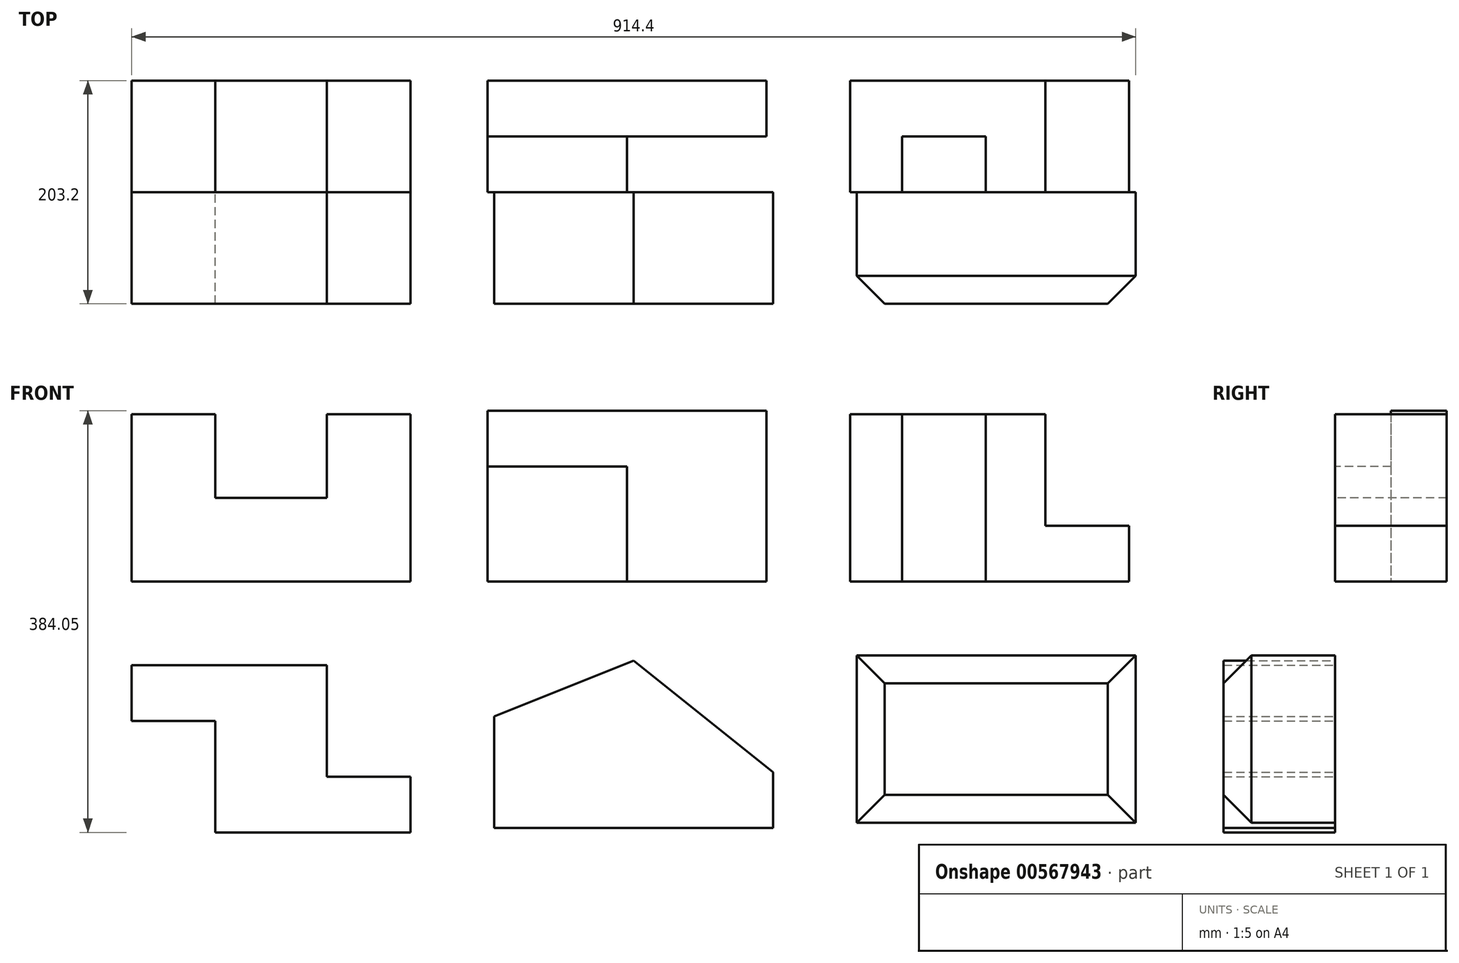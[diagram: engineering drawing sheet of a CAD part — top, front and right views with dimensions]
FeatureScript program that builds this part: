
annotation { "Feature Type Name" : "Feature", "Feature Type Description" : "" }
export const myFeature = defineFeature(function(context is Context, id is Id, definition is map)
    precondition{}
    {
        {
            var Q0;
            Q0=qCreatedBy(makeId("Front.planeOp"),FACE);
            var sketch = newSketch(context, id + "F0", { "sketchPlane" : qUnion([Q0])});
            skLineSegment(sketch, "E0", {"start": v(0, 0) * mm, "end": v(254, 0) * mm});
            skLineSegment(sketch, "E1", {"start": v(254, 0) * mm, "end": v(254, 152.4) * mm});
            skLineSegment(sketch, "E2", {"start": v(254, 152.4) * mm, "end": v(177.8, 152.4) * mm});
            skLineSegment(sketch, "E3", {"start": v(177.8, 152.4) * mm, "end": v(177.8, 76.2) * mm});
            skLineSegment(sketch, "E4", {"start": v(177.8, 76.2) * mm, "end": v(76.2, 76.2) * mm});
            skLineSegment(sketch, "E5", {"start": v(76.2, 76.2) * mm, "end": v(76.2, 152.4) * mm});
            skLineSegment(sketch, "E6", {"start": v(76.2, 152.4) * mm, "end": v(0, 152.4) * mm});
            skLineSegment(sketch, "E7", {"start": v(0, 152.4) * mm, "end": v(0, 0) * mm});
            skSolve(sketch);
        }
        {
            var Q0;
            Q0 = qSketchRegion(id + "F0", true);
            extrude(context, id + "F1", {"entities" : qUnion([Q0]), "oppositeDirection" : true, "depth" : 101.6 * mm, "offsetDistance" : 25.4 * mm});
        }
        {
            var Q0;
            Q0=qCreatedBy(makeId("Top.planeOp"),FACE);
            var sketch = newSketch(context, id + "F2", { "sketchPlane" : qUnion([Q0])});
            skLineSegment(sketch, "E8", {"start": v(323.96, 0) * mm, "end": v(323.96, 101.6) * mm});
            skLineSegment(sketch, "E9", {"start": v(323.96, 101.6) * mm, "end": v(577.96, 101.6) * mm});
            skLineSegment(sketch, "E10", {"start": v(577.96, 101.6) * mm, "end": v(577.96, 50.8) * mm});
            skLineSegment(sketch, "E11", {"start": v(577.96, 50.8) * mm, "end": v(450.96, 50.8) * mm});
            skLineSegment(sketch, "E12", {"start": v(450.96, 50.8) * mm, "end": v(450.96, 0) * mm});
            skLineSegment(sketch, "E13", {"start": v(450.96, 0) * mm, "end": v(323.96, 0) * mm});
            skSolve(sketch);
        }
        {
            var Q0;
            Q0=makeQuery(id+"F2.imprint","IMPRINT",FACE,{"disambiguationData":[TD([[makeQuery(id+"F2.imprint","IMPRINT",EDGE,{"derivedFrom":sQuery(id+"F2.wireOp",EDGE,"E8")}),-1.0]])]});
            extrude(context, id + "F3", {"entities" : qUnion([Q0]), "depth" : 155.45 * mm, "offsetDistance" : 25.4 * mm});
        }
        {
            var Q0;
            Q0=makeQuery(id+"F3.opExtrude","SWEPT_FACE",FACE,{"disambiguationData":[OSD([sQuery(id+"F2.wireOp",EDGE,"E13")])]});
            var sketch = newSketch(context, id + "F4", { "sketchPlane" : qUnion([Q0])});
            skLineSegment(sketch, "E14.bottom", {"start": v(323.96, 155.45) * mm, "end": v(450.96, 155.45) * mm});
            skLineSegment(sketch, "E14.top", {"start": v(323.96, 119.83) * mm, "end": v(450.96, 119.83) * mm});
            skLineSegment(sketch, "E14.left", {"start": v(323.96, 155.45) * mm, "end": v(323.96, 119.83) * mm});
            skLineSegment(sketch, "E14.right", {"start": v(450.96, 155.45) * mm, "end": v(450.96, 119.83) * mm});
            skSolve(sketch);
        }
        {
            var Q0;
            Q0 = qSketchRegion(id + "F4", true);
            extrude(context, id + "F5", {"entities" : qUnion([Q0]), "operationType" : NewBodyOperationType.ADD, "oppositeDirection" : true, "depth" : 50.8 * mm, "offsetDistance" : 25.4 * mm});
        }
        {
            var Q0;
            Q0=makeQuery(id+"F3.opExtrude","SWEPT_FACE",FACE,{"disambiguationData":[OSD([sQuery(id+"F2.wireOp",EDGE,"E13")])]});
            var sketch = newSketch(context, id + "F6", { "sketchPlane" : qUnion([Q0])});
            skLineSegment(sketch, "E15.bottom", {"start": v(323.96, 155.45) * mm, "end": v(450.96, 155.45) * mm});
            skLineSegment(sketch, "E15.top", {"start": v(323.96, 104.65) * mm, "end": v(450.96, 104.65) * mm});
            skLineSegment(sketch, "E15.left", {"start": v(323.96, 155.45) * mm, "end": v(323.96, 104.65) * mm});
            skLineSegment(sketch, "E15.right", {"start": v(450.96, 155.45) * mm, "end": v(450.96, 104.65) * mm});
            skSolve(sketch);
        }
        {
            var Q0;
            Q0=makeQuery(id+"F6.imprint","IMPRINT",FACE,{"disambiguationData":[TD([[makeQuery(id+"F6.imprint","IMPRINT",EDGE,{"derivedFrom":sQuery(id+"F6.wireOp",EDGE,"E15.bottom")}),1.0]])]});
            extrude(context, id + "F7", {"entities" : qUnion([Q0]), "operationType" : NewBodyOperationType.REMOVE, "oppositeDirection" : true, "depth" : 50.8 * mm, "offsetDistance" : 25.4 * mm});
        }
        {
            var Q0;
            Q0=qCreatedBy(makeId("Front.planeOp"),FACE);
            var sketch = newSketch(context, id + "F8", { "sketchPlane" : qUnion([Q0])});
            skLineSegment(sketch, "E16", {"start": v(654.16, 0) * mm, "end": v(654.16, 152.4) * mm});
            skLineSegment(sketch, "E17", {"start": v(654.16, 0) * mm, "end": v(908.16, 0) * mm});
            skLineSegment(sketch, "E18", {"start": v(908.16, 0) * mm, "end": v(908.16, 50.8) * mm});
            skLineSegment(sketch, "E19", {"start": v(908.16, 50.8) * mm, "end": v(831.96, 50.8) * mm});
            skLineSegment(sketch, "E20", {"start": v(831.96, 50.8) * mm, "end": v(831.96, 152.4) * mm});
            skLineSegment(sketch, "E21", {"start": v(831.96, 152.4) * mm, "end": v(654.16, 152.4) * mm});
            skSolve(sketch);
        }
        {
            var Q0;
            Q0=makeQuery(id+"F8.imprint","IMPRINT",FACE,{"disambiguationData":[TD([[makeQuery(id+"F8.imprint","IMPRINT",EDGE,{"derivedFrom":sQuery(id+"F8.wireOp",EDGE,"E16")}),-1.0]])]});
            extrude(context, id + "F9", {"entities" : qUnion([Q0]), "oppositeDirection" : true, "depth" : 101.6 * mm, "offsetDistance" : 25.4 * mm});
        }
        {
            var Q0;
            Q0=makeQuery(id+"F9.opExtrude","SWEPT_FACE",FACE,{"disambiguationData":[OSD([sQuery(id+"F8.wireOp",EDGE,"E21")])]});
            var sketch = newSketch(context, id + "F10", { "sketchPlane" : qUnion([Q0])});
            skLineSegment(sketch, "E22.bottom", {"start": v(701.62, 0) * mm, "end": v(777.82, 0) * mm});
            skLineSegment(sketch, "E22.top", {"start": v(701.62, 50.8) * mm, "end": v(777.82, 50.8) * mm});
            skLineSegment(sketch, "E22.left", {"start": v(701.62, 0) * mm, "end": v(701.62, 50.8) * mm});
            skLineSegment(sketch, "E22.right", {"start": v(777.82, 0) * mm, "end": v(777.82, 50.8) * mm});
            skSolve(sketch);
        }
        {
            var Q0;
            Q0=makeQuery(id+"F10.imprint","IMPRINT",FACE,{"disambiguationData":[TD([[makeQuery(id+"F10.imprint","IMPRINT",EDGE,{"derivedFrom":sQuery(id+"F10.wireOp",EDGE,"E22.bottom")}),-1.0]])]});
            extrude(context, id + "F11", {"entities" : qUnion([Q0]), "operationType" : NewBodyOperationType.REMOVE, "oppositeDirection" : true, "depth" : 152.4 * mm, "offsetDistance" : 25.4 * mm});
        }
        {
            var Q0;
            Q0=qCreatedBy(makeId("Front.planeOp"),FACE);
            var sketch = newSketch(context, id + "F12", { "sketchPlane" : qUnion([Q0])});
            skLineSegment(sketch, "E23", {"start": v(0, -76.2) * mm, "end": v(177.8, -76.2) * mm});
            skLineSegment(sketch, "E24", {"start": v(177.8, -76.2) * mm, "end": v(177.8, -177.8) * mm});
            skLineSegment(sketch, "E25", {"start": v(177.8, -177.8) * mm, "end": v(254, -177.8) * mm});
            skLineSegment(sketch, "E26", {"start": v(254, -177.8) * mm, "end": v(254, -228.6) * mm});
            skLineSegment(sketch, "E27", {"start": v(254, -228.6) * mm, "end": v(76.2, -228.6) * mm});
            skLineSegment(sketch, "E28", {"start": v(76.2, -228.6) * mm, "end": v(76.2, -127) * mm});
            skLineSegment(sketch, "E29", {"start": v(76.2, -127) * mm, "end": v(0, -127) * mm});
            skLineSegment(sketch, "E30", {"start": v(0, -127) * mm, "end": v(0, -76.2) * mm});
            skSolve(sketch);
        }
        {
            var Q0;
            Q0=makeQuery(id+"F12.imprint","IMPRINT",FACE,{"disambiguationData":[TD([[makeQuery(id+"F12.imprint","IMPRINT",EDGE,{"derivedFrom":sQuery(id+"F12.wireOp",EDGE,"E23")}),-1.0]])]});
            extrude(context, id + "F13", {"entities" : qUnion([Q0]), "depth" : 101.6 * mm, "offsetDistance" : 25.4 * mm});
        }
        {
            var Q0;
            Q0=qCreatedBy(makeId("Front.planeOp"),FACE);
            var sketch = newSketch(context, id + "F14", { "sketchPlane" : qUnion([Q0])});
            skLineSegment(sketch, "E31", {"start": v(330.2, -224.58) * mm, "end": v(457.2, -224.58) * mm});
            skLineSegment(sketch, "E32", {"start": v(330.2, -224.58) * mm, "end": v(330.2, -122.98) * mm});
            skLineSegment(sketch, "E33", {"start": v(457.2, -224.58) * mm, "end": v(457.2, -72.18) * mm});
            skLineSegment(sketch, "E34", {"start": v(457.2, -72.18) * mm, "end": v(330.2, -122.98) * mm});
            skLineSegment(sketch, "E35", {"start": v(457.2, -224.58) * mm, "end": v(584.2, -224.58) * mm});
            skLineSegment(sketch, "E36", {"start": v(584.2, -224.58) * mm, "end": v(584.2, -173.78) * mm});
            skLineSegment(sketch, "E37", {"start": v(457.2, -72.18) * mm, "end": v(584.2, -173.78) * mm});
            skSolve(sketch);
        }
        {
            var Q0;
            Q0=makeQuery(id+"F14.imprint","IMPRINT",FACE,{"disambiguationData":[TD([[makeQuery(id+"F14.imprint","IMPRINT",EDGE,{"derivedFrom":sQuery(id+"F14.wireOp",EDGE,"E31")}),1.0]])]});
            var Q1;
            Q1=makeQuery(id+"F14.imprint","IMPRINT",FACE,{"disambiguationData":[TD([[makeQuery(id+"F14.imprint","IMPRINT",EDGE,{"derivedFrom":sQuery(id+"F14.wireOp",EDGE,"E33")}),-1.0]])]});
            extrude(context, id + "F15", {"entities" : qUnion([Q0, Q1]), "depth" : 101.6 * mm, "offsetDistance" : 25.4 * mm});
        }
        {
            var Q0;
            Q0=qCreatedBy(makeId("Front.planeOp"),FACE);
            var sketch = newSketch(context, id + "F16", { "sketchPlane" : qUnion([Q0])});
            skLineSegment(sketch, "E38", {"start": v(660.4, -219.95) * mm, "end": v(914.4, -219.95) * mm});
            skLineSegment(sketch, "E39", {"start": v(660.4, -219.95) * mm, "end": v(660.4, -67.55) * mm});
            skLineSegment(sketch, "E40", {"start": v(660.4, -219.95) * mm, "end": v(660.4, -219.95) * mm});
            skPoint(sketch, "E40.endSnap0", {"position": v(787.4, -219.95) * mm});
            skLineSegment(sketch, "E41", {"start": v(914.4, -219.95) * mm, "end": v(914.4, -67.55) * mm});
            skLineSegment(sketch, "E42", {"start": v(660.4, -67.55) * mm, "end": v(914.4, -67.55) * mm});
            skSolve(sketch);
        }
        {
            var Q0;
            Q0=makeQuery(id+"F16.imprint","IMPRINT",FACE,{"disambiguationData":[TD([[makeQuery(id+"F16.imprint","IMPRINT",EDGE,{"derivedFrom":sQuery(id+"F16.wireOp",EDGE,"E38")}),1.0]])]});
            extrude(context, id + "F17", {"entities" : qUnion([Q0]), "depth" : 101.6 * mm, "offsetDistance" : 25.4 * mm});
        }
        {
            var Q0;
            Q0=makeQuery(id+"F17.opExtrude","CAP_FACE",FACE,{"disambiguationData":[OSD([sQuery(id+"F16.wireOp",EDGE,"E38"),sQuery(id+"F16.wireOp",EDGE,"E39"),sQuery(id+"F16.wireOp",EDGE,"E41"),sQuery(id+"F16.wireOp",EDGE,"E42")])],"isStart":false});
            extrude(context, id + "F18", {"entities" : qUnion([Q0]), "operationType" : NewBodyOperationType.ADD, "oppositeDirection" : true, "depth" : 25.4 * mm, "offsetDistance" : 25.4 * mm});
        }
        {
            var Q0;
            Q0=makeQuery(id+"F17.opExtrude","CAP_FACE",FACE,{"disambiguationData":[OSD([sQuery(id+"F16.wireOp",EDGE,"E38"),sQuery(id+"F16.wireOp",EDGE,"E39"),sQuery(id+"F16.wireOp",EDGE,"E41"),sQuery(id+"F16.wireOp",EDGE,"E42")])],"isStart":false});
            chamfer(context, id + "F19", {"entities" : qUnion([Q0]), "width" : 25.4 * mm, "tangentPropagation" : true});
        }
    });
